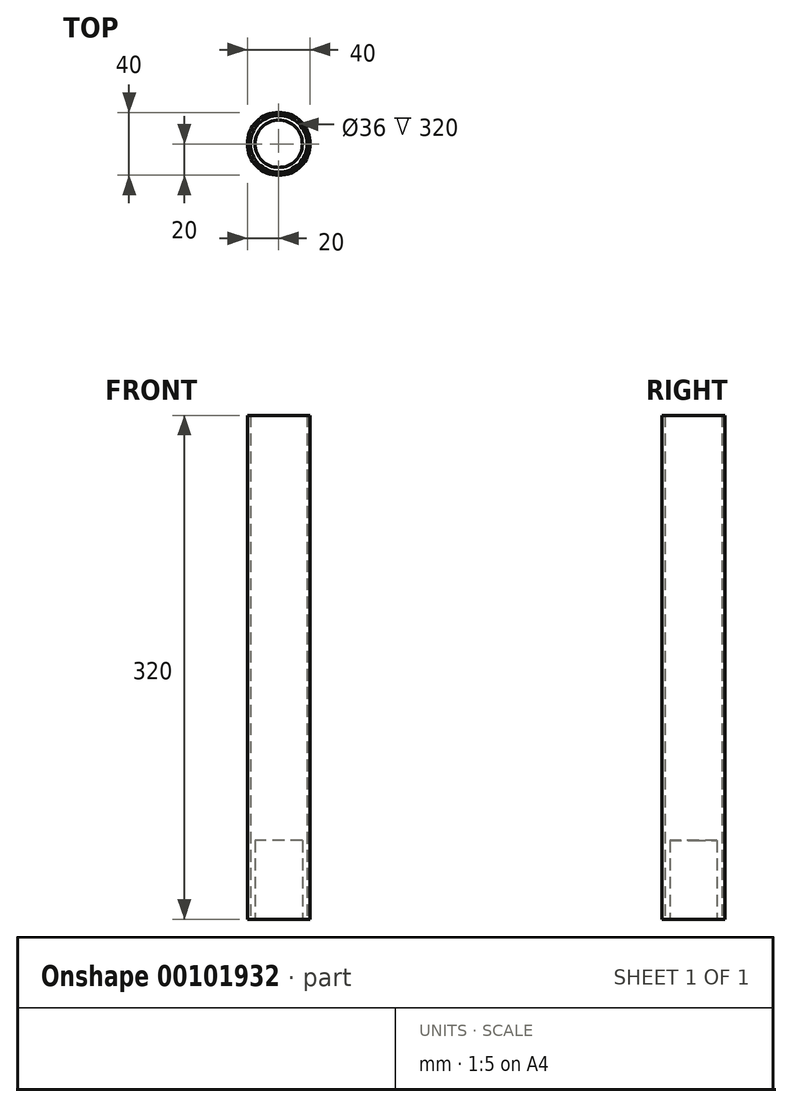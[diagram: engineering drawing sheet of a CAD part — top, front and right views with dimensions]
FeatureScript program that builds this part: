
annotation { "Feature Type Name" : "Feature", "Feature Type Description" : "" }
export const myFeature = defineFeature(function(context is Context, id is Id, definition is map)
    precondition{}
    {
        {
            var Q0;
            Q0=qCreatedBy(makeId("Top.planeOp"),FACE);
            var sketch = newSketch(context, id + "F0", { "sketchPlane" : qUnion([Q0])});
            skCircle(sketch, "E0", {"center": v(0, 0) * mm, "radius": 18 * mm});
            skCircle(sketch, "E1", {"center": v(0, 0) * mm, "radius": 20 * mm});
            skSolve(sketch);
        }
        {
            var Q0;
            Q0=qCreatedBy(makeId("Top.planeOp"),FACE);
            var sketch = newSketch(context, id + "F1", { "sketchPlane" : qUnion([Q0])});
            skCircle(sketch, "E2", {"center": v(0, 0) * mm, "radius": 15 * mm});
            skSolve(sketch);
        }
        {
            var Q0;
            Q0 = qSketchRegion(id + "F0", true);
            extrude(context, id + "F2", {"entities" : qUnion([Q0]), "depth" : 320 * mm});
        }
        {
            var Q0;
            Q0 = qSketchRegion(id + "F1", true);
            extrude(context, id + "F3", {"entities" : qUnion([Q0]), "depth" : 50 * mm});
        }
    });
